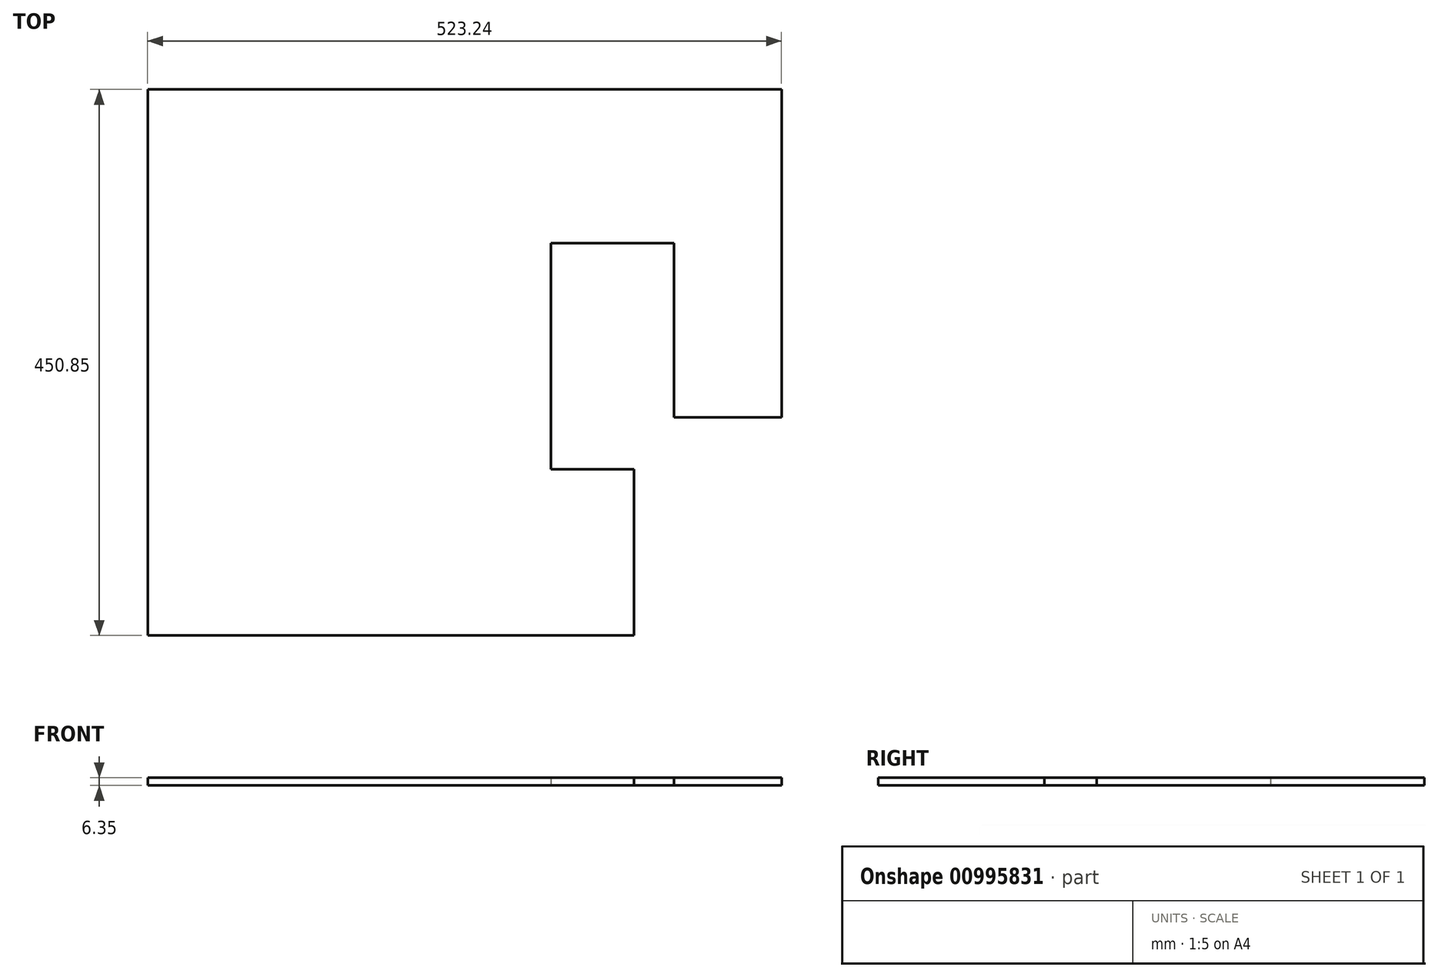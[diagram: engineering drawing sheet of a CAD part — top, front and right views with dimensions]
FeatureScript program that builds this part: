
annotation { "Feature Type Name" : "Feature", "Feature Type Description" : "" }
export const myFeature = defineFeature(function(context is Context, id is Id, definition is map)
    precondition{}
    {
        {
            var Q0;
            Q0=qCreatedBy(makeId("Top.planeOp"),FACE);
            var sketch = newSketch(context, id + "F0", { "sketchPlane" : qUnion([Q0])});
            skLineSegment(sketch, "E0", {"start": v(494.88, 0) * mm, "end": v(-28.36, 0) * mm});
            skLineSegment(sketch, "E1", {"start": v(-28.36, 0) * mm, "end": v(-28.36, -450.85) * mm});
            skLineSegment(sketch, "E2", {"start": v(-28.36, -450.85) * mm, "end": v(372.96, -450.85) * mm});
            skLineSegment(sketch, "E3", {"start": v(372.96, -450.85) * mm, "end": v(372.96, -313.7) * mm});
            skLineSegment(sketch, "E4", {"start": v(372.96, -313.7) * mm, "end": v(304.38, -313.7) * mm});
            skLineSegment(sketch, "E5", {"start": v(304.38, -313.7) * mm, "end": v(304.38, -127) * mm});
            skLineSegment(sketch, "E6", {"start": v(304.38, -127) * mm, "end": v(405.98, -127) * mm});
            skLineSegment(sketch, "E7", {"start": v(405.98, -270.76) * mm, "end": v(494.88, -270.76) * mm});
            skLineSegment(sketch, "E8", {"start": v(494.88, -270.76) * mm, "end": v(494.88, 0) * mm});
            skLineSegment(sketch, "E9", {"start": v(405.98, -270.76) * mm, "end": v(405.98, -127) * mm});
            skSolve(sketch);
        }
        {
            var Q0;
            Q0=makeQuery(id+"F0.imprint","IMPRINT",FACE,{"disambiguationData":[TD([[makeQuery(id+"F0.imprint","IMPRINT",EDGE,{"derivedFrom":sQuery(id+"F0.wireOp",EDGE,"E0")}),1.0]])]});
            extrude(context, id + "F1", {"entities" : qUnion([Q0]), "depth" : 6.35 * mm, "offsetDistance" : 25.4 * mm});
        }
    });
